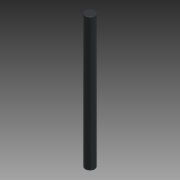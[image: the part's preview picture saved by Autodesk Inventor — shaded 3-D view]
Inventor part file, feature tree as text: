
AUTODESK INVENTOR PART (.ipt)
format: ipt  version: 2020 (Build 240168000, 168)  size: 76,288 bytes
history: native  units: mm
features: extrude x1, chamfer x1, sketch x1
ambient origin geometry x8: Origin, YZ Plane, XZ Plane, XY Plane, X Axis, Y Axis, Z Axis, Center Point
bodies: Solid1 (feature_tree)
feature tree (3):
  extrude  "Extrusion1"  Depth=360.0mm TaperAngle=0.0deg
  chamfer  "Chamfer1"  Distance=1.0mm Angle=45.0deg
  sketch  "Sketch1"  dims[d0=25.4mm d1=360.0mm d2=0.0mm d3=1.0mm d4=2.0mm d5=45.0deg]
